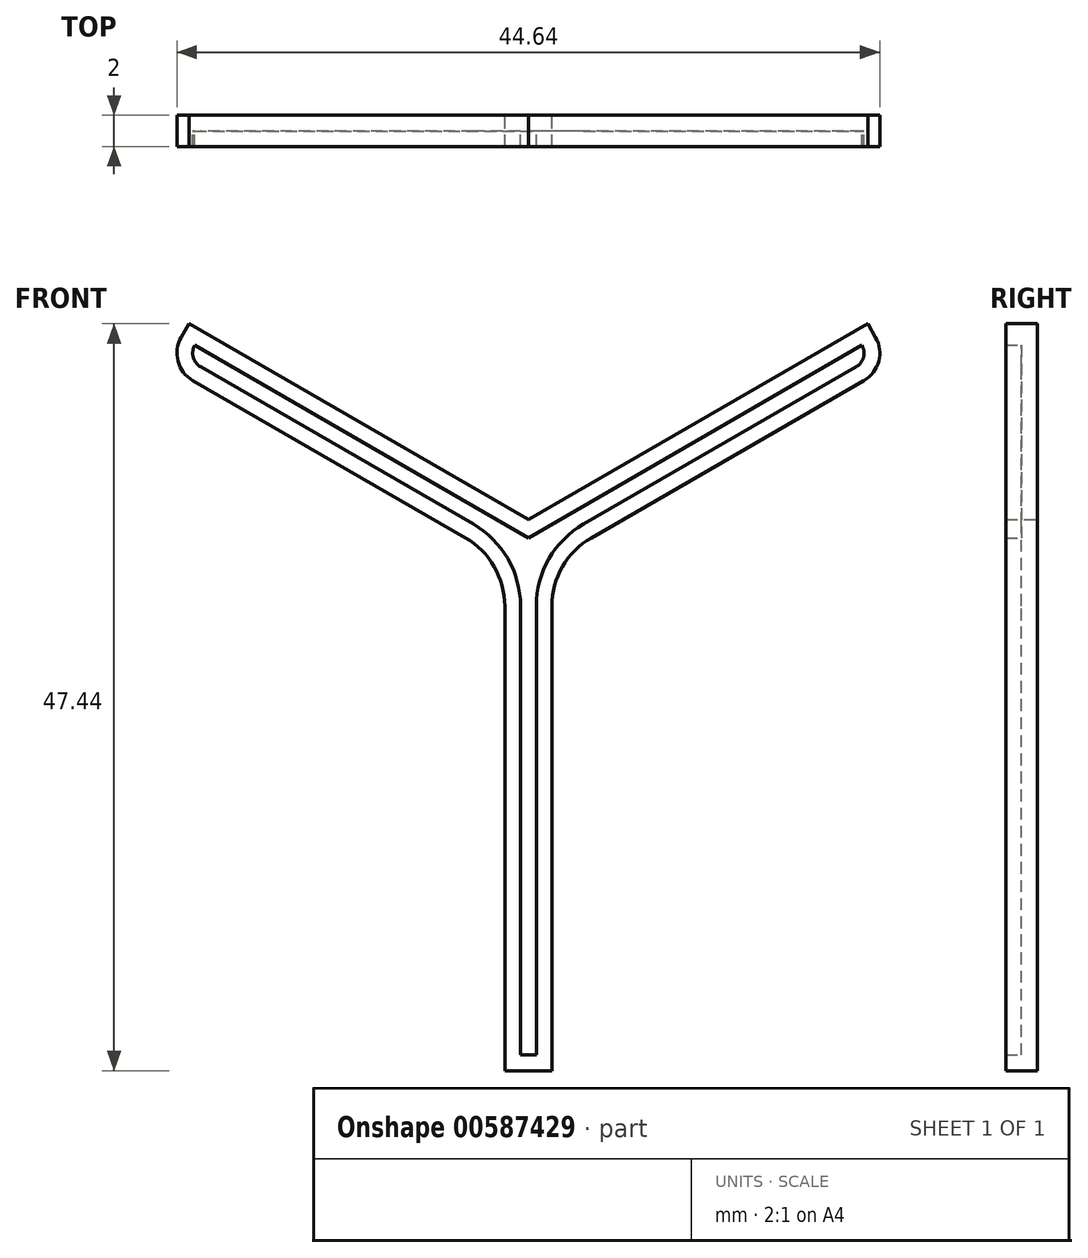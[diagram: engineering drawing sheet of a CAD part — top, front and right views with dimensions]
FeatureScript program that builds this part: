
annotation { "Feature Type Name" : "Feature", "Feature Type Description" : "" }
export const myFeature = defineFeature(function(context is Context, id is Id, definition is map)
    precondition{}
    {
        {
            var Q0;
            Q0=qCreatedBy(makeId("Front.planeOp"),FACE);
            var sketch = newSketch(context, id + "F0", { "sketchPlane" : qUnion([Q0])});
            skLineSegment(sketch, "E0.bottom", {"start": v(0, 0) * mm, "end": v(3, 0) * mm});
            skLineSegment(sketch, "E0.left", {"start": v(0, 0) * mm, "end": v(0, 29.52) * mm});
            skLineSegment(sketch, "E0.right", {"start": v(3, 0) * mm, "end": v(3, 29.52) * mm});
            skLineSegment(sketch, "E1", {"start": v(5.5, 33.85) * mm, "end": v(22.82, 43.85) * mm});
            skLineSegment(sketch, "E2", {"start": v(23.55, 46.58) * mm, "end": v(23.05, 47.44) * mm});
            skLineSegment(sketch, "E3", {"start": v(23.05, 47.44) * mm, "end": v(1.5, 35) * mm});
            skLineSegment(sketch, "E4", {"start": v(-2.5, 33.85) * mm, "end": v(-19.82, 43.85) * mm});
            skLineSegment(sketch, "E5", {"start": v(-20.55, 46.58) * mm, "end": v(-20.05, 47.44) * mm});
            skLineSegment(sketch, "E6", {"start": v(-20.05, 47.44) * mm, "end": v(1.5, 35) * mm});
            skPoint(sketch, "E7.visualSharp", {"position": v(1.5, 35) * mm});
            skPoint(sketch, "E8.visualSharp", {"position": v(3, 32.4) * mm});
            skArc(sketch, "E8.filletArc", {"start": v(5.5, 33.85) * mm, "mid": v(3.67, 32.02) * mm, "end": v(3, 29.52) * mm});
            skPoint(sketch, "E9.visualSharp", {"position": v(0, 32.4) * mm});
            skArc(sketch, "E9.filletArc", {"start": v(0, 29.52) * mm, "mid": v(-0.67, 32.02) * mm, "end": v(-2.5, 33.85) * mm});
            skPoint(sketch, "E10.visualSharp", {"position": v(-21.55, 44.85) * mm});
            skArc(sketch, "E10.filletArc", {"start": v(-20.55, 46.58) * mm, "mid": v(-20.75, 45.06) * mm, "end": v(-19.82, 43.85) * mm});
            skPoint(sketch, "E11.visualSharp", {"position": v(24.55, 44.85) * mm});
            skArc(sketch, "E11.filletArc", {"start": v(22.82, 43.85) * mm, "mid": v(23.75, 45.06) * mm, "end": v(23.55, 46.58) * mm});
            skSolve(sketch);
        }
        {
            var Q0;
            Q0 = qSketchRegion(id + "F0", true);
            extrude(context, id + "F1", {"entities" : qUnion([Q0]), "endBound" : BoundingType.SYMMETRIC, "depth" : 2 * mm, "offsetDistance" : 25 * mm});
        }
        {
            var Q0;
            Q0=makeQuery(id+"F1.opExtrude","CAP_FACE",FACE,{"disambiguationData":[OSD([sQuery(id+"F0.wireOp",EDGE,"E0.bottom"),sQuery(id+"F0.wireOp",EDGE,"E0.left"),sQuery(id+"F0.wireOp",EDGE,"E0.right"),sQuery(id+"F0.wireOp",EDGE,"E1"),sQuery(id+"F0.wireOp",EDGE,"E2"),sQuery(id+"F0.wireOp",EDGE,"E3"),sQuery(id+"F0.wireOp",EDGE,"E4"),sQuery(id+"F0.wireOp",EDGE,"E5"),sQuery(id+"F0.wireOp",EDGE,"E6"),sQuery(id+"F0.wireOp",EDGE,"E8.filletArc"),sQuery(id+"F0.wireOp",EDGE,"E9.filletArc"),sQuery(id+"F0.wireOp",EDGE,"E10.filletArc"),sQuery(id+"F0.wireOp",EDGE,"E11.filletArc")])],"isStart":false});
            shell(context, id + "F2", {"entities" : qUnion([Q0]), "thickness" : 1 * mm});
        }
    });
